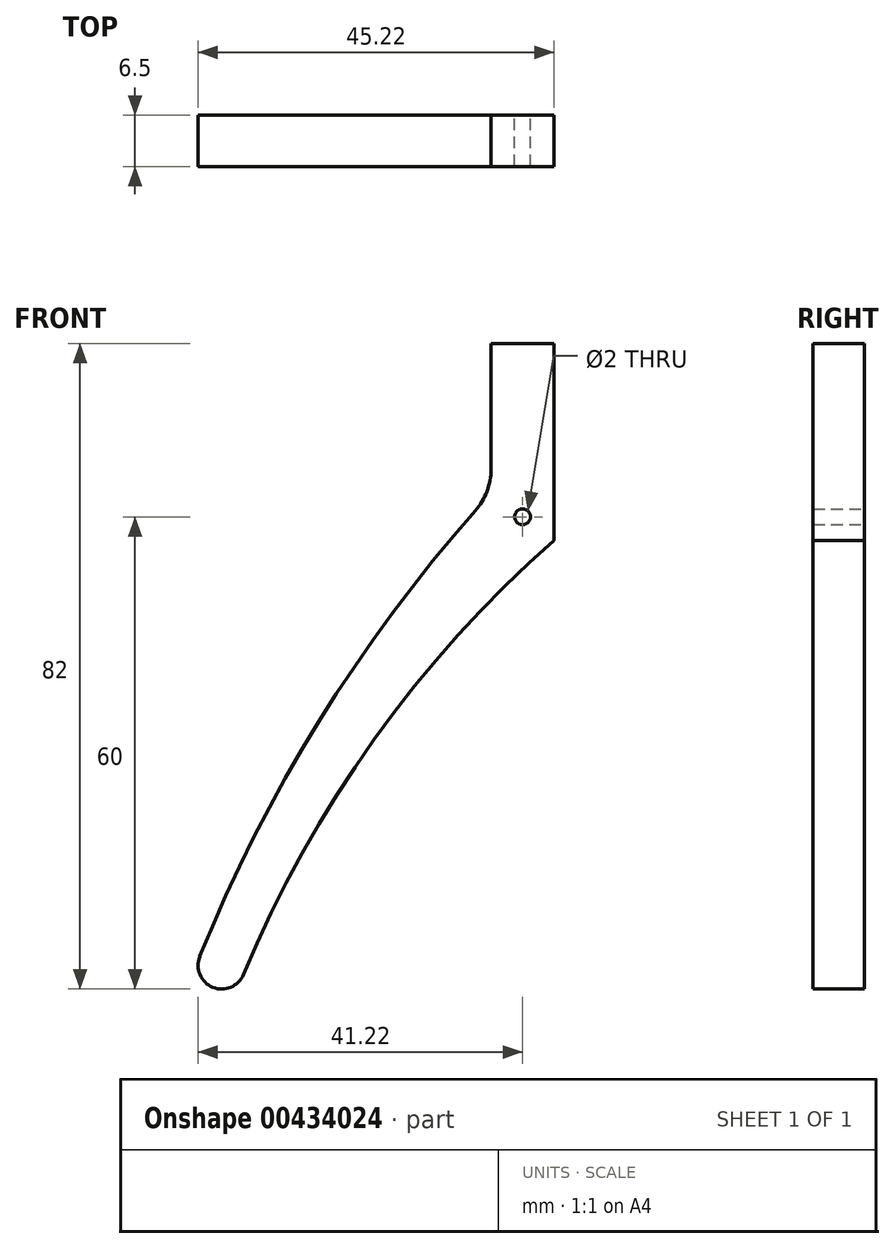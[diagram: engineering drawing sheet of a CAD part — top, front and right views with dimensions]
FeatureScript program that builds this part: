
annotation { "Feature Type Name" : "Feature", "Feature Type Description" : "" }
export const myFeature = defineFeature(function(context is Context, id is Id, definition is map)
    precondition{}
    {
        {
            var Q0;
            Q0=qCreatedBy(makeId("Front.planeOp"),FACE);
            var sketch = newSketch(context, id + "F0", { "sketchPlane" : qUnion([Q0])});
            skLineSegment(sketch, "E0.bottom", {"start": v(-4, -9.5) * mm, "end": v(4, -9.5) * mm});
            skLineSegment(sketch, "E0.top", {"start": v(-4, 9.5) * mm, "end": v(4, 9.5) * mm});
            skLineSegment(sketch, "E0.left", {"start": v(-4, -6.44) * mm, "end": v(-4, 9.5) * mm});
            skLineSegment(sketch, "E0.right", {"start": v(4, -9.5) * mm, "end": v(4, 9.5) * mm});
            skPoint(sketch, "E0.middle", {"position": v(0, 0) * mm});
            skCircle(sketch, "E1", {"center": v(-38.22, -69.5) * mm, "radius": 3 * mm});
            skArc(sketch, "E2", {"start": v(-6, -11.73) * mm, "mid": v(-25.9, -38.57) * mm, "end": v(-41, -68.38) * mm});
            skLineSegment(sketch, "E3", {"start": v(4, -9.5) * mm, "end": v(4, -15.5) * mm});
            skPoint(sketch, "E4.visualSharp", {"position": v(-4, -9.5) * mm});
            skArc(sketch, "E4.filletArc", {"start": v(-6, -11.73) * mm, "mid": v(-4.52, -9.27) * mm, "end": v(-4, -6.44) * mm});
            skArc(sketch, "E5", {"start": v(4, -15.5) * mm, "mid": v(-18.88, -40.82) * mm, "end": v(-35.44, -70.65) * mm});
            skCircle(sketch, "E6", {"center": v(0, -12.5) * mm, "radius": 1 * mm});
            skSolve(sketch);
        }
        {
            var Q0;
            {var subQ0=sQuery(id+"F0.wireOp",EDGE,"E1");var subQ1=makeQuery(id+"F0.imprint","INTERSECT",VERTEX,{"derivedFrom":[subQ0,sQuery(id+"F0.wireOp",EDGE,"E2")]});Q0=makeQuery(id+"F0.imprint","IMPRINT",FACE,{"disambiguationData":[TD([[makeQuery(id+"F0.imprint","IMPRINT",EDGE,{"disambiguationData":[TD([[subQ1,-1.0]])],"derivedFrom":subQ0}),1.0]])]});}
            var Q1;
            Q1=makeQuery(id+"F0.imprint","IMPRINT",FACE,{"disambiguationData":[TD([[makeQuery(id+"F0.imprint","IMPRINT",EDGE,{"derivedFrom":sQuery(id+"F0.wireOp",EDGE,"E0.top")}),-1.0]])]});
            extrude(context, id + "F1", {"entities" : qUnion([Q0, Q1]), "depth" : 6.5 * mm});
        }
    });
